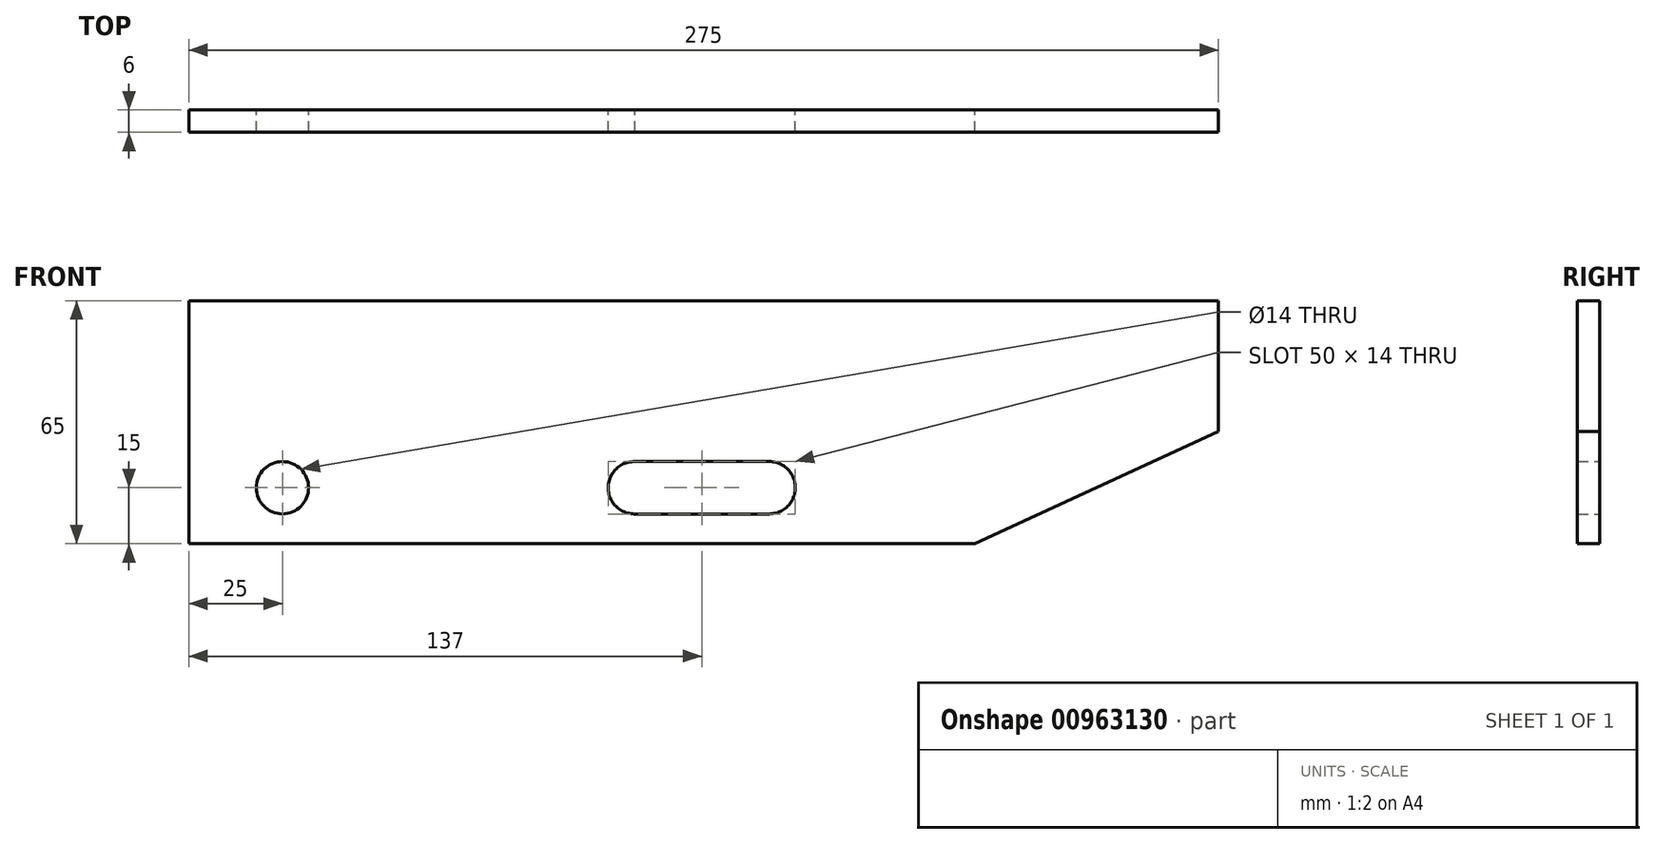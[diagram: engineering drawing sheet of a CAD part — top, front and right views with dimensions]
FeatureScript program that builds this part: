
annotation { "Feature Type Name" : "Feature", "Feature Type Description" : "" }
export const myFeature = defineFeature(function(context is Context, id is Id, definition is map)
    precondition{}
    {
        {
            var Q0;
            Q0=qCreatedBy(makeId("Front.planeOp"),FACE);
            var sketch = newSketch(context, id + "F0", { "sketchPlane" : qUnion([Q0])});
            skLineSegment(sketch, "E0", {"start": v(0, 0) * mm, "end": v(0, -65) * mm});
            skLineSegment(sketch, "E1", {"start": v(0, 0) * mm, "end": v(0, -50) * mm, "construction": true});
            skLineSegment(sketch, "E2", {"start": v(0, -50) * mm, "end": v(25, -50) * mm, "construction": true});
            skLineSegment(sketch, "E3", {"start": v(25, -50) * mm, "end": v(137, -50) * mm, "construction": true});
            skLineSegment(sketch, "E4", {"start": v(0, 0) * mm, "end": v(275, 0) * mm});
            skLineSegment(sketch, "E5", {"start": v(275, 0) * mm, "end": v(275, -35) * mm});
            skCircle(sketch, "E6", {"center": v(25, -50) * mm, "radius": 7 * mm});
            skLineSegment(sketch, "E7", {"start": v(137, -50) * mm, "end": v(155, -50) * mm, "construction": true});
            skArc(sketch, "E8", {"start": v(155, -57) * mm, "mid": v(162, -50) * mm, "end": v(155, -43) * mm});
            skLineSegment(sketch, "E9", {"start": v(137, -50) * mm, "end": v(119, -50) * mm});
            skArc(sketch, "E10", {"start": v(119.18, -43) * mm, "mid": v(112, -49.93) * mm, "end": v(119.05, -57) * mm});
            skLineSegment(sketch, "E11", {"start": v(0, -65) * mm, "end": v(210, -65) * mm});
            skLineSegment(sketch, "E12", {"start": v(210, -65) * mm, "end": v(275, -35) * mm});
            skLineSegment(sketch, "E13", {"start": v(118.82, -43) * mm, "end": v(155, -43) * mm});
            skLineSegment(sketch, "E14", {"start": v(119.05, -57) * mm, "end": v(155, -57) * mm});
            skSolve(sketch);
        }
        {
            var Q0;
            Q0=makeQuery(id+"F0.imprint","IMPRINT",FACE,{"disambiguationData":[TD([[makeQuery(id+"F0.imprint","IMPRINT",EDGE,{"derivedFrom":sQuery(id+"F0.wireOp",EDGE,"E0")}),1.0]])]});
            extrude(context, id + "F1", {"entities" : qUnion([Q0]), "depth" : 6 * mm, "offsetDistance" : 25 * mm});
        }
    });
